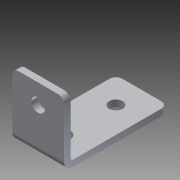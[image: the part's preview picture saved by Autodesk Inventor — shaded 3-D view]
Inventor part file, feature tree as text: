
AUTODESK INVENTOR PART (.ipt)
format: ipt  version: 2013 (Build 170138000, 138)  size: 130,048 bytes
history: native  units: in
note: dims shown in document units (in); Inventor stores cm internally (conversion verified against a paired STEP export)
features: sheet_metal_op x4, sketch x3, other x3, chamfer x1
ambient origin geometry x8: Origin, YZ Plane, XZ Plane, XY Plane, X Axis, Y Axis, Z Axis, Center Point
feature tree (11):
  sheet_metal_op  "Face1"
  sheet_metal_op  "Flange1"
  chamfer  "Corner Round1"
  sketch  "Sketch1"  dims[d0=2.0in]
  other  "Plate1"
  sketch  "Sketch2"  dims[d1=1.0in]
  other  "Plate2"
  sheet_metal_op  "Bend1"
  sheet_metal_op  "Corner1"
  sketch  "Sketch3"  dims[d2=0.26in d3=0.26in d4=1.0in d8=0.125in d9=0.125in d10=0.0625in d11=0.25in d12=0.125in d13=1.25in d14=90.0deg d15=0.05in d16=0.5in d17=0.125in d18=0.125in d19=0.26in d21=0.875in d22=0.125in d23=0.0in d24=0.125in]
  other  "Cut1"
